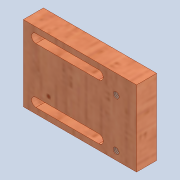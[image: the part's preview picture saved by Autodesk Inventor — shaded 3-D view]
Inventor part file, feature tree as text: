
AUTODESK INVENTOR PART (.ipt)
format: ipt  version: 2020 (Build 240168000, 168)  size: 152,064 bytes
history: native  units: mm
features: sketch x3, other x3, extrude x2, reference x2, hole x1
ambient origin geometry x8: Origin, YZ Plane, XZ Plane, XY Plane, X Axis, Y Axis, Z Axis, Center Point
bodies: Solid1 (feature_tree)
feature tree (11):
  extrude  "Extrusion1"  Depth=30.0mm
  extrude  "Extrusion5"  Depth=3.5mm
  hole  "Hole1"  [1 undecoded]
  sketch  "Sketch1"  dims[d0=45.0mm d1=30.0mm]
  sketch  "Sketch5"  dims[d2=8.0mm d3=0.0mm d29=3.5mm]
  sketch  "Sketch6"  dims[d30=4.0mm d31=4.0mm d33=25.0mm d34=10.0mm d35=0.0mm d36=5.0mm d37=2.459mm d38=8.0mm d39=4.0mm d40=2.0mm d41=90.0deg d42=8.0mm d43=20.594885mm]
  reference  "Reference1"
  reference  "Reference2"
  parser-record x1  (decoder bookkeeping rows leaked as tree rows — omitted from the tree; the rows remain in map.json)
  other  "0005-00-00 Ansamblu_General_V1.iam"
  other  "0005-20-1003 Switch:2"
note: 1 required parameter value undecoded (feature->parameter linkage not recoverable at this tier; creation-order binding heuristic only, values carry confidence <= 0.55)
note: 1 file-system path scrubbed to <path> (originals preserved in map.json)
